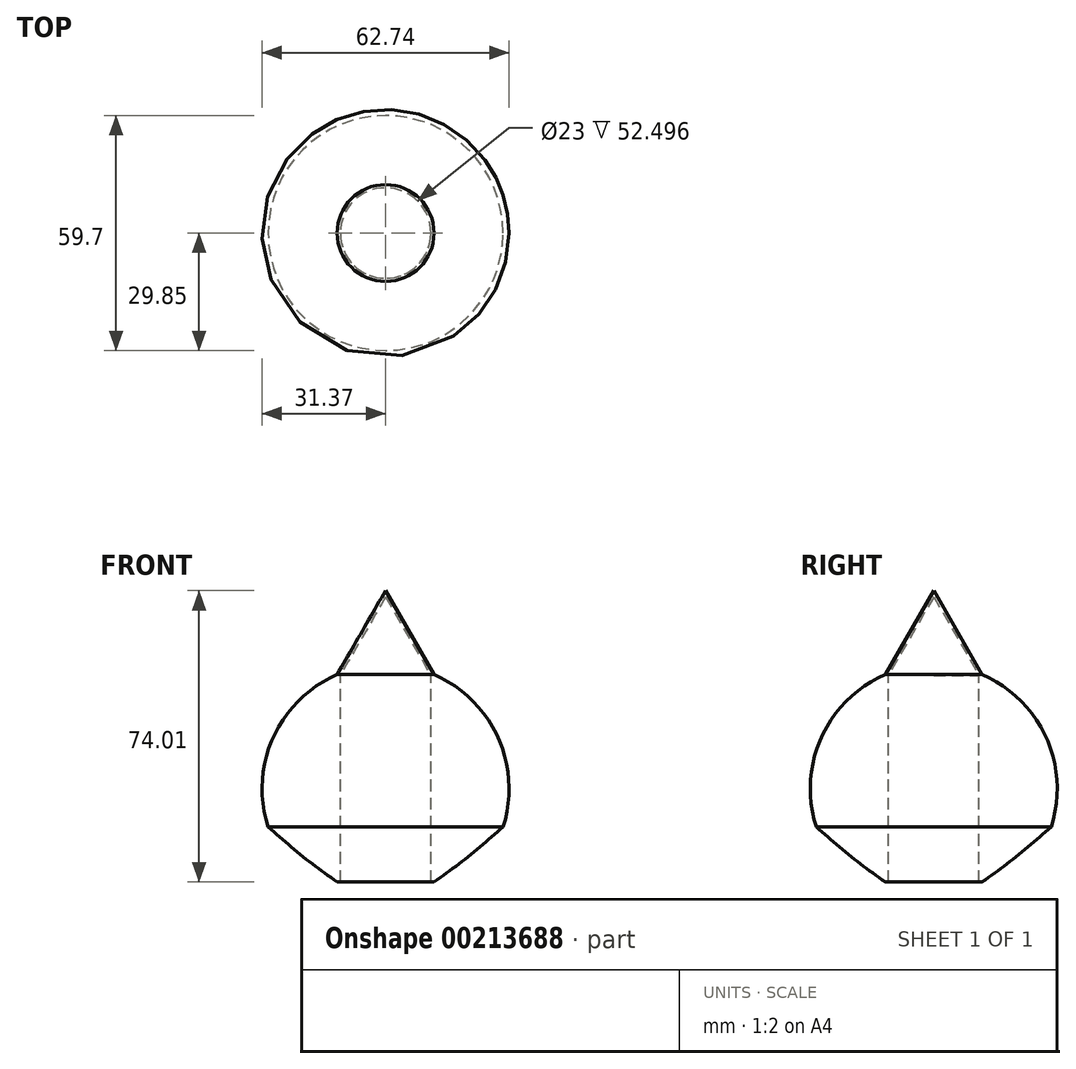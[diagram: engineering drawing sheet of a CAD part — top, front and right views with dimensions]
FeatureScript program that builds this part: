
annotation { "Feature Type Name" : "Feature", "Feature Type Description" : "" }
export const myFeature = defineFeature(function(context is Context, id is Id, definition is map)
    precondition{}
    {
        {
            var Q0;
            Q0=qCreatedBy(makeId("Front.planeOp"),FACE);
            var sketch = newSketch(context, id + "F0", { "sketchPlane" : qUnion([Q0])});
            skLineSegment(sketch, "E0", {"start": v(-12.3, 52.71) * mm, "end": v(0, 74.01) * mm});
            skLineSegment(sketch, "E1", {"start": v(0, 74.01) * mm, "end": v(0, 72.41) * mm});
            skLineSegment(sketch, "E2", {"start": v(0, 72.41) * mm, "end": v(-11.5, 52.5) * mm});
            skLineSegment(sketch, "E3", {"start": v(-11.5, 52.5) * mm, "end": v(-11.5, 0) * mm});
            skLineSegment(sketch, "E4", {"start": v(-11.5, 0) * mm, "end": v(-12.3, 0) * mm});
            skLineSegment(sketch, "E5", {"start": v(-6.15, 63.36) * mm, "end": v(-5.46, 62.96) * mm, "construction": true});
            skArc(sketch, "E6", {"start": v(-12.3, 52.71) * mm, "mid": v(-28.55, 36.74) * mm, "end": v(-29.85, 14) * mm});
            skArc(sketch, "E7", {"start": v(-29.85, 14) * mm, "mid": v(-21.3, 6.7) * mm, "end": v(-12.3, 0) * mm});
            skSolve(sketch);
        }
        {
            var Q0;
            Q0 = qSketchRegion(id + "F0", true);
            var Q1;
            Q1=sQuery(id+"F0.wireOp",EDGE,"E1");
            revolve(context, id + "F1", {"entities" : qUnion([Q0]), "axis" : qUnion([Q1]), "revolveType" : RevolveType.FULL});
        }
    });
